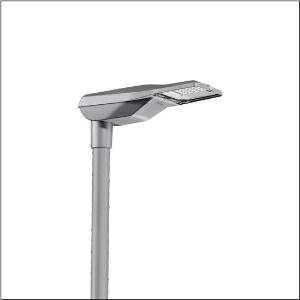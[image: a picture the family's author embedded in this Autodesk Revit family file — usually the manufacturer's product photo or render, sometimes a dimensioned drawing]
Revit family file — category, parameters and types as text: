
# Revit family: streetlight_sl_21_iq_micro___stw1_0a_5xe1e31d08db_99ec
name_source: partatom
category: Lighting Fixtures
units: mm (PartAtom-declared; Revit-internal decimal feet)

## family parameters
Cut with Voids When Loaded = No
Host = Face
Light Source = No
Part Type = Normal
Room Calculation Point = No
Round Connector Dimension = Use Diameter
Shared = No

## types (1)
- --- (1 x LED, 4810 lm, 36.4 W, 3000K)
    Apparent Load = 36 VA
    CIE Flux Codes = 38 75 98 100 100
    Color Rendering = 70
    Color Temperature = 3000K
    Default Elevation = 1800 mm
    Description = Streetlight SL 21 iQ micro, mast luminaire, primary light control with lens, of PMMA, primary optical cover: cover, of toughened safety glass, transparent, light distribution: STW1.0a, light emission: direct distribution, primary light characteristic: asymmetric, installation type: post-top, side-entry, LED, High Power LED, rated luminous flux: 4.810lm, luminous efficacy: 132lm/W, light colour: 730, colour temperature: 3000K, control: Auto-Match, Temp-Guard, Lumen-Switch, Night-Set, Smart-Wire, Light-Fading, Desk-Remote (wireless, voltage-free reading and setting of iQ features in the workshop via application-optimized NFC function/RFID function), optimised constant luminous flux control (CLO 2.0), presetting dimming linear, mains connection: 220..240V, AC, 50/60Hz, start of lifetime: 36W, end of service life: 38W, reduction: 16W, luminaire housing, of diecast aluminium, powder-coated, Siteco® metallic grey (DB 702S), corrosivity category C5 mid according to DIN EN ISO 12944, please order mast flange separately, inclination adjustable: 0°, 5°, 10°, 15°, sealing non-destructively replaceable, multi-level sealing system, length: 528mm, width: 235mm, height: 110mm, mast flange for spigot size: 42mm (side-entry): 5XC10008XM4, 60/48mm (side-entry/post-top): 5XC10108XM2, 76/60mm (side-entry/post-top): 5XC10108XM1, protection rating (complete): IP66, insulation class (complete): insulation class II (safety insulation), certification: CE, ENEC, ENEC+, VDE, impact resistance: IK09, permissible operating ambient temperature for outdoor applications: -40..+50°C, standard-compliant lighting for roads and squares, packaging unit: 1 piece

Light Distribution: STW1.0a
    Height = 110 mm
    Lamp = 1 x LED
    Lamp Light Flux = 4810 lm
    Lamp Power = 36.4 W
    Lamp count = 1
    Length = 528 mm
    Luminous efficacy = 132 lm/W
    Manufacturer = Siteco
    ModVariant = No
    Model = 5XE1E31D08DB
    Number of Poles = 1
    OnlyDefault = Yes
    Power Factor = 1
    Product Name = Streetlight SL 21 iQ micro | STW1.0a
    Product group = mast luminaire | pylon top
    ProductGroupID = 6100
    Protection Class = Protection class II
    Protection Degree = IP 66
    RLX_Detail_Level = 1
    RLX_Emergency_Light_Flux = 0 lm
    RLX_Emergency_Type = 0
    RLX_Emergency_Type_DB = No
    RlxData = <blob elided: 99113 chars, md5=16ef87cd>
    Socket = socket
    Standby Power = 0 W
    System Light Flux = 4810 lm
    System Power = 36 W
    Type Comments = factory setting: luminous flux: 100 % | dim-lin: 254 | 715 mA
    Type Image = l_1006881.jpg
    URL = http://relux.com
    VarID = @adj_087803
    Voltage = 0 V
    Weight = 0.00 kg
    Width = 235 mm

## geometry (parser evidence)
native form markers: Blend x4, Sweep x11
no freeform markers — native parametric forms only
